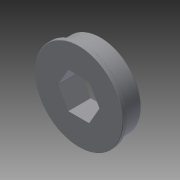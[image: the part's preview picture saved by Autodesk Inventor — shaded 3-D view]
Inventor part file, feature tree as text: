
AUTODESK INVENTOR PART (.ipt)
format: ipt  version: 2014 SP1 (Build 180222100, 222)  size: 140,288 bytes
history: native  units: in
note: dims shown in document units (in); Inventor stores cm internally (conversion verified against a paired STEP export)
features: fillet x1, other x1, imported_body x1
ambient origin geometry x8: Origin, YZ Plane, XZ Plane, XY Plane, X Axis, Y Axis, Z Axis, Center Point
bodies: Body1 (feature_tree)
feature tree (3):
  fillet  "Fillet2"  [1 undecoded]
  other  "FR8ZZ Hex Bearing.ipt1"
  imported_body  "Base1"
note: 1 required parameter value undecoded (feature->parameter linkage not recoverable at this tier; creation-order binding heuristic only, values carry confidence <= 0.55)
